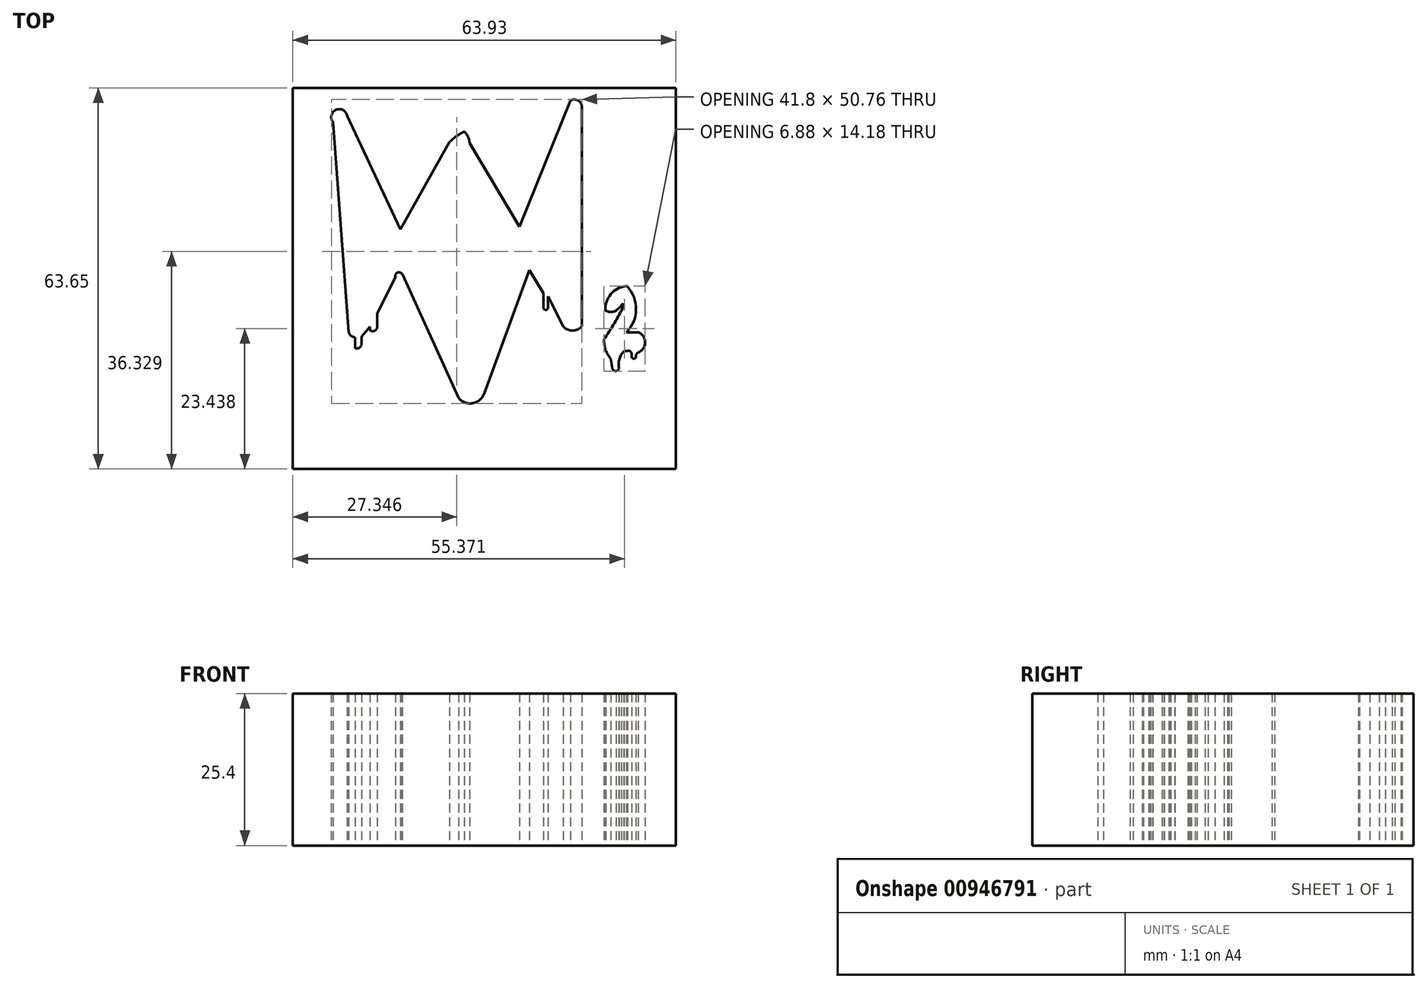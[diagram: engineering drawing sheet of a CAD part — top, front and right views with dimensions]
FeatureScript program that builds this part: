
annotation { "Feature Type Name" : "Feature", "Feature Type Description" : "" }
export const myFeature = defineFeature(function(context is Context, id is Id, definition is map)
    precondition{}
    {
        {
            var Q0;
            Q0=qCreatedBy(makeId("Top.planeOp"),FACE);
            var sketch = newSketch(context, id + "F0", { "sketchPlane" : qUnion([Q0])});
            skLineSegment(sketch, "E0", {"start": v(-6.92, 26.97) * mm, "end": v(12.58, -14.61) * mm});
            skLineSegment(sketch, "E1", {"start": v(12.58, -14.61) * mm, "end": v(30.34, 29.56) * mm});
            skArc(sketch, "E2", {"start": v(32.27, 28.53) * mm, "mid": v(31.58, 29.56) * mm, "end": v(30.34, 29.56) * mm});
            skLineSegment(sketch, "E3", {"start": v(32.27, 28.53) * mm, "end": v(32.27, -8.17) * mm});
            skArc(sketch, "E4", {"start": v(29.12, -8.17) * mm, "mid": v(30.7, -8.88) * mm, "end": v(32.27, -8.17) * mm});
            skLineSegment(sketch, "E5", {"start": v(29.12, -8.17) * mm, "end": v(26.63, -3.14) * mm});
            skLineSegment(sketch, "E6", {"start": v(26.63, -3.14) * mm, "end": v(26.63, -5.02) * mm});
            skArc(sketch, "E7", {"start": v(25.83, -5.02) * mm, "mid": v(26.23, -5.42) * mm, "end": v(26.63, -5.02) * mm});
            skLineSegment(sketch, "E8", {"start": v(25.83, -5.02) * mm, "end": v(25.83, -2.63) * mm});
            skLineSegment(sketch, "E9", {"start": v(25.83, -2.63) * mm, "end": v(23.48, 1.23) * mm});
            skLineSegment(sketch, "E10", {"start": v(23.48, 1.23) * mm, "end": v(15.91, -19.45) * mm});
            skArc(sketch, "E11", {"start": v(11.69, -20.1) * mm, "mid": v(14, -21.03) * mm, "end": v(15.91, -19.45) * mm});
            skLineSegment(sketch, "E12", {"start": v(11.69, -20.1) * mm, "end": v(2.29, 0.57) * mm});
            skArc(sketch, "E13", {"start": v(2.29, 0) * mm, "mid": v(1.72, 0.85) * mm, "end": v(1.16, 0) * mm});
            skLineSegment(sketch, "E14", {"start": v(1.16, 0) * mm, "end": v(-1.9, -6.01) * mm});
            skLineSegment(sketch, "E15", {"start": v(-1.9, -6.01) * mm, "end": v(-1.9, -8.22) * mm});
            skArc(sketch, "E16", {"start": v(-3.11, -8.83) * mm, "mid": v(-2.32, -8.9) * mm, "end": v(-1.9, -8.22) * mm});
            skLineSegment(sketch, "E17", {"start": v(-3.11, -8.83) * mm, "end": v(-3.11, -8.22) * mm});
            skLineSegment(sketch, "E18", {"start": v(-3.11, -8.22) * mm, "end": v(-4.52, -9.91) * mm});
            skLineSegment(sketch, "E19", {"start": v(-4.52, -9.91) * mm, "end": v(-4.52, -11.09) * mm});
            skArc(sketch, "E20", {"start": v(-5.6, -11.84) * mm, "mid": v(-4.87, -11.75) * mm, "end": v(-4.52, -11.09) * mm});
            skLineSegment(sketch, "E21", {"start": v(-5.6, -11.84) * mm, "end": v(-5.6, -10) * mm});
            skArc(sketch, "E22", {"start": v(-6.64, -9.11) * mm, "mid": v(-6.28, -9.74) * mm, "end": v(-5.6, -10) * mm});
            skLineSegment(sketch, "E23", {"start": v(-6.64, -9.11) * mm, "end": v(-9.27, 25.94) * mm});
            skArc(sketch, "E24", {"start": v(-6.92, 26.97) * mm, "mid": v(-8.77, 28) * mm, "end": v(-9.27, 25.94) * mm});
            skLineSegment(sketch, "E25", {"start": v(0, 4.42) * mm, "end": v(-4.38, -2.3) * mm});
            skLineSegment(sketch, "E26", {"start": v(-4.38, -2.3) * mm, "end": v(-6.45, 17.58) * mm});
            skLineSegment(sketch, "E27", {"start": v(-6.45, 17.58) * mm, "end": v(0, 4.42) * mm});
            skLineSegment(sketch, "E28", {"start": v(1.96, 8.03) * mm, "end": v(10.2, 22.62) * mm});
            skArc(sketch, "E29", {"start": v(12.65, 24.35) * mm, "mid": v(11.35, 23.6) * mm, "end": v(10.2, 22.62) * mm});
            skArc(sketch, "E30", {"start": v(13.53, 22.45) * mm, "mid": v(13.26, 23.48) * mm, "end": v(12.65, 24.35) * mm});
            skLineSegment(sketch, "E31", {"start": v(13.53, 22.45) * mm, "end": v(21.87, 8.49) * mm});
            skArc(sketch, "E32", {"start": v(39.67, -1.46) * mm, "mid": v(37.1, -2.79) * mm, "end": v(36.19, -5.53) * mm});
            skArc(sketch, "E33", {"start": v(39.67, -9.17) * mm, "mid": v(41.3, -5.34) * mm, "end": v(39.8, -1.46) * mm});
            skLineSegment(sketch, "E34", {"start": v(39.67, -9.17) * mm, "end": v(41.68, -9.17) * mm});
            skArc(sketch, "E35", {"start": v(41.68, -12.53) * mm, "mid": v(42.83, -10.85) * mm, "end": v(41.68, -9.17) * mm});
            skArc(sketch, "E36", {"start": v(41.68, -12.53) * mm, "mid": v(41.32, -12.9) * mm, "end": v(41.29, -13.42) * mm});
            skArc(sketch, "E37", {"start": v(40.56, -13.42) * mm, "mid": v(40.92, -13.56) * mm, "end": v(41.29, -13.42) * mm});
            skLineSegment(sketch, "E38", {"start": v(40.56, -13.42) * mm, "end": v(40.56, -12.76) * mm});
            skArc(sketch, "E39", {"start": v(40.56, -12.76) * mm, "mid": v(40.33, -12.34) * mm, "end": v(39.86, -12.29) * mm});
            skLineSegment(sketch, "E40", {"start": v(39.86, -12.29) * mm, "end": v(39.3, -12.29) * mm});
            skArc(sketch, "E41", {"start": v(39.3, -12.29) * mm, "mid": v(38.54, -13.63) * mm, "end": v(38.46, -15.17) * mm});
            skArc(sketch, "E42", {"start": v(37.35, -15.17) * mm, "mid": v(37.9, -15.64) * mm, "end": v(38.46, -15.17) * mm});
            skLineSegment(sketch, "E43", {"start": v(37.35, -15.17) * mm, "end": v(37.1, -13.62) * mm});
            skArc(sketch, "E44", {"start": v(35.95, -10.33) * mm, "mid": v(36.22, -12.08) * mm, "end": v(37.1, -13.62) * mm});
            skArc(sketch, "E45", {"start": v(35.95, -10.33) * mm, "mid": v(37.7, -7.63) * mm, "end": v(39.25, -4.8) * mm});
            skArc(sketch, "E46", {"start": v(39.25, -4.8) * mm, "mid": v(39.06, -4.5) * mm, "end": v(38.88, -4.8) * mm});
            skArc(sketch, "E47", {"start": v(38.88, -4.8) * mm, "mid": v(38.4, -5.16) * mm, "end": v(37.96, -5.57) * mm});
            skArc(sketch, "E48", {"start": v(36.24, -5.57) * mm, "mid": v(37.1, -5.78) * mm, "end": v(37.96, -5.57) * mm});
            skLineSegment(sketch, "E49", {"start": v(36.19, -5.53) * mm, "end": v(36.24, -5.57) * mm});
            skLineSegment(sketch, "E50.bottom", {"start": v(-15.98, 31.66) * mm, "end": v(47.95, 31.66) * mm});
            skLineSegment(sketch, "E50.top", {"start": v(-15.98, -32) * mm, "end": v(47.95, -32) * mm});
            skLineSegment(sketch, "E50.left", {"start": v(-15.98, 31.66) * mm, "end": v(-15.98, -32) * mm});
            skLineSegment(sketch, "E50.right", {"start": v(47.95, 31.66) * mm, "end": v(47.95, -32) * mm});
            skLineSegment(sketch, "E51", {"start": v(29.34, 18.5) * mm, "end": v(29.34, -2.65) * mm});
            skLineSegment(sketch, "E52", {"start": v(29.34, -2.65) * mm, "end": v(24.6, 4.45) * mm});
            skLineSegment(sketch, "E53", {"start": v(24.6, 4.45) * mm, "end": v(29.34, 18.5) * mm});
            skLineSegment(sketch, "E54", {"start": v(3.22, 5.35) * mm, "end": v(11.83, 19.27) * mm});
            skLineSegment(sketch, "E55", {"start": v(11.83, 19.27) * mm, "end": v(20.8, 5.82) * mm});
            skLineSegment(sketch, "E56", {"start": v(39.67, -1.46) * mm, "end": v(39.8, -1.46) * mm});
            skLineSegment(sketch, "E57", {"start": v(2.29, 0.57) * mm, "end": v(2.18, 0.64) * mm});
            skSolve(sketch);
        }
        {
            var Q0;
            {var subQ4=sQuery(id+"F0.wireOp",EDGE,"E2");Q0=makeQuery(id+"F0.imprint","IMPRINT",FACE,{"disambiguationData":[TD([[makeQuery(id+"F0.imprint","IMPRINT",EDGE,{"derivedFrom":subQ4}),-1.0]])]});}
            extrude(context, id + "F1", {"entities" : qUnion([Q0]), "depth" : 25.4 * mm, "offsetDistance" : 25.4 * mm});
        }
    });
